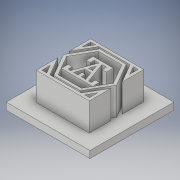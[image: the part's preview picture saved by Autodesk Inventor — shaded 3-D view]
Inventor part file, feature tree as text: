
AUTODESK INVENTOR PART (.ipt)
format: ipt  version: 2019 (Build 230136000, 136)  size: 228,352 bytes
history: native  units: mm
features: extrude x2, sketch x2
ambient origin geometry x8: Origin, YZ Plane, XZ Plane, XY Plane, X Axis, Y Axis, Z Axis, Center Point
bodies: Solid1 (feature_tree)
feature tree (4):
  extrude  "Extrusion1"  Depth=20.0mm
  extrude  "Extrusion2"  Depth=1.0mm
  sketch  "Sketch1"  dims[d0=20.0mm d1=20.0mm]
  sketch  "Sketch2"  dims[d2=0.5mm d3=1.0mm d4=1.5mm d5=1.0mm d6=1.5mm d7=1.0mm d9=12.217305mm d13=1.5mm d14=1.5mm d15=1.0mm d16=1.0mm d17=2.0mm d18=1.0mm d19=2.5mm d23=1.0mm d26=2.5mm d27=10.0mm d28=0.0mm d29=0.5mm d30=1.0mm d32=1.0mm d33=1.0mm d34=1.0mm d35=30.0mm d36=30.0mm d37=2.5mm d38=0.0mm]
